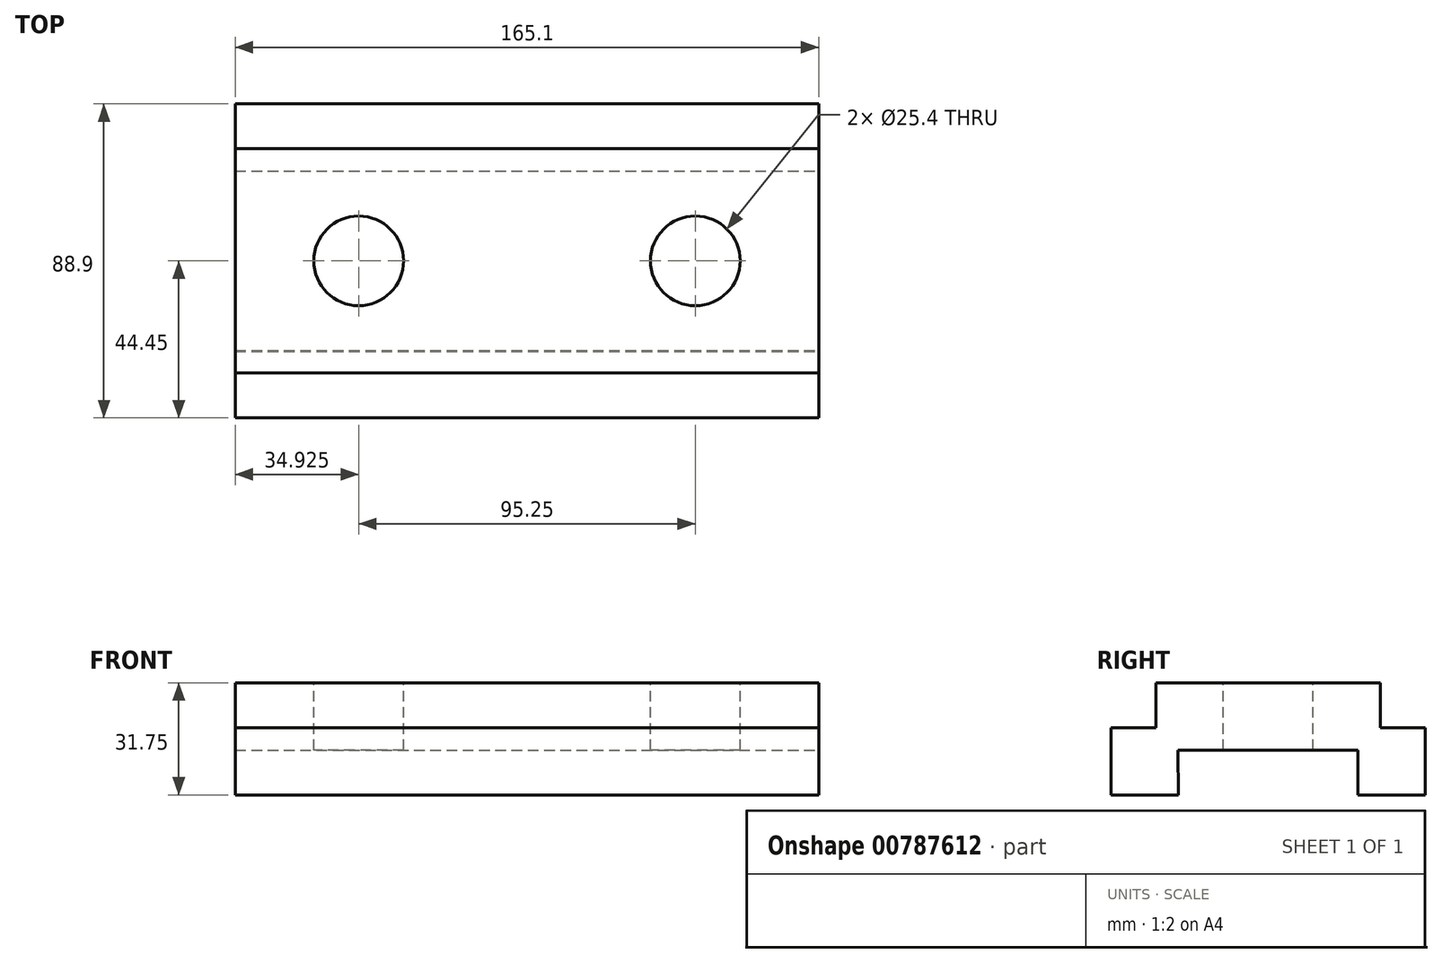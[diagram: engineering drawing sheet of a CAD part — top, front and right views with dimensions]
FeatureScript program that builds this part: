
annotation { "Feature Type Name" : "Feature", "Feature Type Description" : "" }
export const myFeature = defineFeature(function(context is Context, id is Id, definition is map)
    precondition{}
    {
        {
            var Q0;
            Q0=qCreatedBy(makeId("Front.planeOp"),FACE);
            var sketch = newSketch(context, id + "F0", { "sketchPlane" : qUnion([Q0])});
            skLineSegment(sketch, "E0", {"start": v(0, 0) * mm, "end": v(165.1, 0) * mm});
            skLineSegment(sketch, "E1", {"start": v(165.1, 0) * mm, "end": v(165.1, -31.75) * mm});
            skLineSegment(sketch, "E2", {"start": v(165.1, -31.75) * mm, "end": v(0, -31.75) * mm});
            skLineSegment(sketch, "E3", {"start": v(0, -31.75) * mm, "end": v(0, 0) * mm});
            skSolve(sketch);
        }
        {
            var Q0;
            Q0=makeQuery(id+"F0.imprint","IMPRINT",FACE,{"disambiguationData":[TD([[makeQuery(id+"F0.imprint","IMPRINT",EDGE,{"derivedFrom":sQuery(id+"F0.wireOp",EDGE,"E0")}),-1.0]])]});
            extrude(context, id + "F1", {"entities" : qUnion([Q0]), "depth" : 88.9 * mm, "offsetDistance" : 25.4 * mm});
        }
        {
            var Q0;
            Q0=makeQuery(id+"F1.opExtrude","SWEPT_FACE",FACE,{"disambiguationData":[OSD([sQuery(id+"F0.wireOp",EDGE,"E1")])]});
            var sketch = newSketch(context, id + "F2", { "sketchPlane" : qUnion([Q0])});
            skLineSegment(sketch, "E4", {"start": v(-88.9, -31.75) * mm, "end": v(-69.85, -31.75) * mm});
            skLineSegment(sketch, "E5", {"start": v(0, -31.75) * mm, "end": v(-19.05, -31.75) * mm});
            skLineSegment(sketch, "E6", {"start": v(-19.05, -31.75) * mm, "end": v(-19.05, -19.05) * mm});
            skLineSegment(sketch, "E7", {"start": v(-19.05, -19.05) * mm, "end": v(-70.03, -19.05) * mm});
            skLineSegment(sketch, "E8", {"start": v(-69.85, -31.75) * mm, "end": v(-70.03, -19.05) * mm});
            skSolve(sketch);
        }
        {
            var Q0;
            {var subQ0=sQuery(id+"F2.wireOp",EDGE,"E6");Q0=makeQuery(id+"F2.imprint","IMPRINT",FACE,{"disambiguationData":[TD([[makeQuery(id+"F2.imprint","IMPRINT",EDGE,{"derivedFrom":subQ0}),1.0]])]});}
            extrude(context, id + "F3", {"entities" : qUnion([Q0]), "operationType" : NewBodyOperationType.REMOVE, "endBound" : BoundingType.THROUGH_ALL, "oppositeDirection" : true, "depth" : 25.4 * mm, "offsetDistance" : 25.4 * mm});
        }
        {
            var Q0;
            Q0=makeQuery(id+"F1.opExtrude","CAP_FACE",FACE,{"disambiguationData":[OSD([sQuery(id+"F0.wireOp",EDGE,"E0"),sQuery(id+"F0.wireOp",EDGE,"E1"),sQuery(id+"F0.wireOp",EDGE,"E2"),sQuery(id+"F0.wireOp",EDGE,"E3")])],"isStart":false});
            var sketch = newSketch(context, id + "F4", { "sketchPlane" : qUnion([Q0])});
            skLineSegment(sketch, "E9", {"start": v(165.1, -31.75) * mm, "end": v(165.1, -12.7) * mm});
            skLineSegment(sketch, "E10", {"start": v(165.1, -12.7) * mm, "end": v(0, -12.7) * mm});
            skSolve(sketch);
        }
        {
            var Q0;
            {var subQ0=sQuery(id+"F4.wireOp",EDGE,"E10");Q0=makeQuery(id+"F4.imprint","IMPRINT",FACE,{"disambiguationData":[TD([[makeQuery(id+"F4.imprint","IMPRINT",EDGE,{"derivedFrom":subQ0}),-1.0]])]});}
            extrude(context, id + "F5", {"entities" : qUnion([Q0]), "operationType" : NewBodyOperationType.REMOVE, "oppositeDirection" : true, "depth" : 12.7 * mm, "offsetDistance" : 25.4 * mm});
        }
        {
            var Q0;
            Q0=makeQuery(id+"F1.opExtrude","CAP_FACE",FACE,{"disambiguationData":[OSD([sQuery(id+"F0.wireOp",EDGE,"E0"),sQuery(id+"F0.wireOp",EDGE,"E1"),sQuery(id+"F0.wireOp",EDGE,"E2"),sQuery(id+"F0.wireOp",EDGE,"E3")])],"isStart":true});
            var sketch = newSketch(context, id + "F6", { "sketchPlane" : qUnion([Q0])});
            skLineSegment(sketch, "E11", {"start": v(-165.1, -31.75) * mm, "end": v(-165.1, -12.7) * mm});
            skLineSegment(sketch, "E12", {"start": v(-165.1, -12.7) * mm, "end": v(0, -12.7) * mm});
            skSolve(sketch);
        }
        {
            var Q0;
            {var subQ0=sQuery(id+"F6.wireOp",EDGE,"E12");Q0=makeQuery(id+"F6.imprint","IMPRINT",FACE,{"disambiguationData":[TD([[makeQuery(id+"F6.imprint","IMPRINT",EDGE,{"derivedFrom":subQ0}),1.0]])]});}
            extrude(context, id + "F7", {"entities" : qUnion([Q0]), "operationType" : NewBodyOperationType.REMOVE, "oppositeDirection" : true, "depth" : 12.7 * mm, "offsetDistance" : 25.4 * mm});
        }
        {
            var Q0;
            Q0=makeQuery(id+"F1.opExtrude","SWEPT_FACE",FACE,{"disambiguationData":[OSD([sQuery(id+"F0.wireOp",EDGE,"E0")])]});
            var sketch = newSketch(context, id + "F8", { "sketchPlane" : qUnion([Q0])});
            skLineSegment(sketch, "E13", {"start": v(0, -44.45) * mm, "end": v(34.93, -44.45) * mm, "construction": true});
            skLineSegment(sketch, "E14", {"start": v(130.18, -44.45) * mm, "end": v(34.93, -44.45) * mm, "construction": true});
            skCircle(sketch, "E15", {"center": v(34.93, -44.45) * mm, "radius": 12.7 * mm});
            skCircle(sketch, "E16", {"center": v(130.18, -44.45) * mm, "radius": 12.7 * mm});
            skSolve(sketch);
        }
        {
            var Q0;
            Q0=makeQuery(id+"F8.imprint","IMPRINT",FACE,{"disambiguationData":[TD([[makeQuery(id+"F8.imprint","IMPRINT",EDGE,{"derivedFrom":sQuery(id+"F8.wireOp",EDGE,"E15")}),1.0]])]});
            var Q1;
            Q1=makeQuery(id+"F8.imprint","IMPRINT",FACE,{"disambiguationData":[TD([[makeQuery(id+"F8.imprint","IMPRINT",EDGE,{"derivedFrom":sQuery(id+"F8.wireOp",EDGE,"E16")}),1.0]])]});
            extrude(context, id + "F9", {"entities" : qUnion([Q0, Q1]), "operationType" : NewBodyOperationType.REMOVE, "endBound" : BoundingType.THROUGH_ALL, "oppositeDirection" : true, "depth" : 25.4 * mm, "offsetDistance" : 25.4 * mm});
        }
    });
